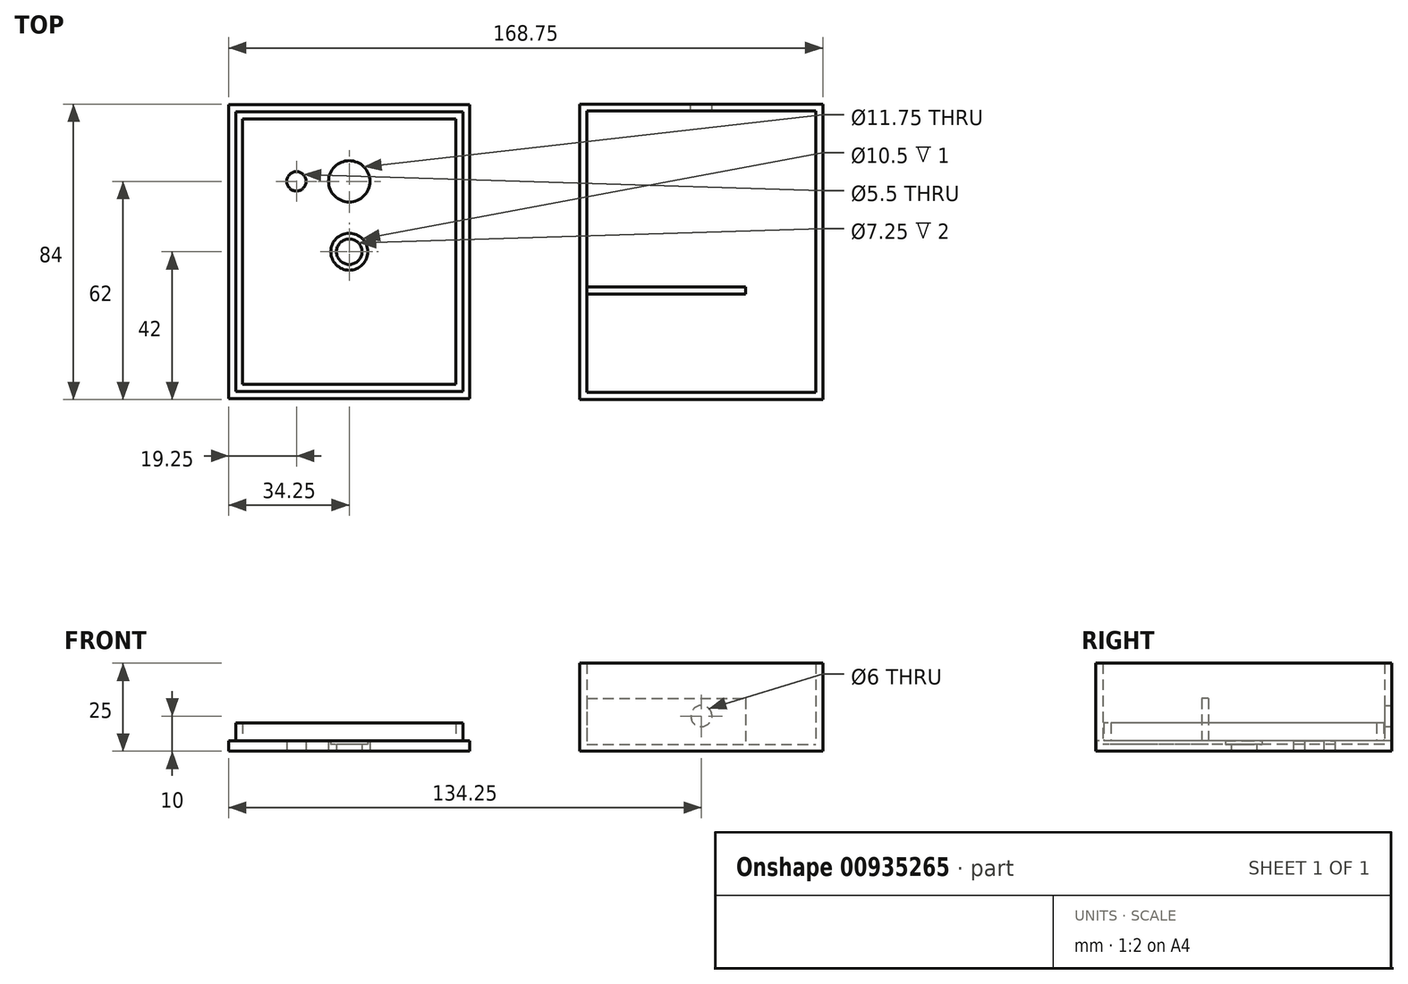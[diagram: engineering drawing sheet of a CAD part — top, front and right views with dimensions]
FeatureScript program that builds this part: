
annotation { "Feature Type Name" : "Feature", "Feature Type Description" : "" }
export const myFeature = defineFeature(function(context is Context, id is Id, definition is map)
    precondition{}
    {
        {
            var Q0;
            Q0=qCreatedBy(makeId("Top.planeOp"),FACE);
            var sketch = newSketch(context, id + "F0", { "sketchPlane" : qUnion([Q0])});
            skLineSegment(sketch, "E0.bottom", {"start": v(-32.5, 40) * mm, "end": v(32.5, 40) * mm});
            skLineSegment(sketch, "E0.top", {"start": v(-32.5, -40) * mm, "end": v(32.5, -40) * mm});
            skLineSegment(sketch, "E0.left", {"start": v(-32.5, 40) * mm, "end": v(-32.5, -40) * mm});
            skLineSegment(sketch, "E0.right", {"start": v(32.5, 40) * mm, "end": v(32.5, -40) * mm});
            skPoint(sketch, "E0.middle", {"position": v(0, 0) * mm});
            skLineSegment(sketch, "E1.0", {"start": v(-34.5, 42) * mm, "end": v(34.5, 42) * mm});
            skLineSegment(sketch, "E1.1", {"start": v(-34.5, 42) * mm, "end": v(-34.5, -42) * mm});
            skLineSegment(sketch, "E1.2", {"start": v(-34.5, -42) * mm, "end": v(34.5, -42) * mm});
            skLineSegment(sketch, "E1.3", {"start": v(34.5, 42) * mm, "end": v(34.5, -42) * mm});
            skLineSegment(sketch, "E2.bottom", {"start": v(-32.5, -10) * mm, "end": v(12.5, -10) * mm});
            skLineSegment(sketch, "E2.top", {"start": v(-32.5, -12) * mm, "end": v(12.5, -12) * mm});
            skLineSegment(sketch, "E2.left", {"start": v(-32.5, -10) * mm, "end": v(-32.5, -12) * mm});
            skLineSegment(sketch, "E2.right", {"start": v(12.5, -10) * mm, "end": v(12.5, -12) * mm});
            skLineSegment(sketch, "E3.bottom", {"start": v(-67.75, 39.75) * mm, "end": v(-132.25, 39.75) * mm});
            skLineSegment(sketch, "E3.top", {"start": v(-67.75, -39.75) * mm, "end": v(-132.25, -39.75) * mm});
            skLineSegment(sketch, "E3.left", {"start": v(-67.75, 39.75) * mm, "end": v(-67.75, -39.75) * mm});
            skLineSegment(sketch, "E3.right", {"start": v(-132.25, 39.75) * mm, "end": v(-132.25, -39.75) * mm});
            skPoint(sketch, "E3.middle", {"position": v(-100, 0) * mm});
            skLineSegment(sketch, "E4.0", {"start": v(-65.75, 41.75) * mm, "end": v(-134.25, 41.75) * mm});
            skLineSegment(sketch, "E4.1", {"start": v(-65.75, 41.75) * mm, "end": v(-65.75, -41.75) * mm});
            skLineSegment(sketch, "E4.2", {"start": v(-65.75, -41.75) * mm, "end": v(-134.25, -41.75) * mm});
            skLineSegment(sketch, "E4.3", {"start": v(-134.25, 41.75) * mm, "end": v(-134.25, -41.75) * mm});
            skLineSegment(sketch, "E5.0", {"start": v(-69.75, 37.75) * mm, "end": v(-130.25, 37.75) * mm});
            skLineSegment(sketch, "E5.1", {"start": v(-69.75, 37.75) * mm, "end": v(-69.75, -37.75) * mm});
            skLineSegment(sketch, "E5.2", {"start": v(-69.75, -37.75) * mm, "end": v(-130.25, -37.75) * mm});
            skLineSegment(sketch, "E5.3", {"start": v(-130.25, 37.75) * mm, "end": v(-130.25, -37.75) * mm});
            skCircle(sketch, "E6", {"center": v(-100, 20) * mm, "radius": 5.88 * mm});
            skCircle(sketch, "E7", {"center": v(-100, 0) * mm, "radius": 3.62 * mm});
            skCircle(sketch, "E8", {"center": v(-100, 0) * mm, "radius": 5.25 * mm});
            skCircle(sketch, "E9", {"center": v(-115, 20) * mm, "radius": 2.75 * mm});
            skSolve(sketch);
        }
        {
            var Q0;
            {var subQ4=sQuery(id+"F0.wireOp",EDGE,"E0.bottom");Q0=makeQuery(id+"F0.imprint","IMPRINT",FACE,{"disambiguationData":[TD([[makeQuery(id+"F0.imprint","IMPRINT",EDGE,{"derivedFrom":subQ4}),-1.0]])]});}
            extrude(context, id + "F1", {"entities" : qUnion([Q0]), "depth" : 2 * mm, "offsetDistance" : 25 * mm});
        }
        {
            var Q0;
            {var subQ3=sQuery(id+"F0.wireOp",EDGE,"E0.bottom");Q0=makeQuery(id+"F0.imprint","IMPRINT",FACE,{"disambiguationData":[TD([[makeQuery(id+"F0.imprint","IMPRINT",EDGE,{"derivedFrom":subQ3}),1.0]])]});}
            extrude(context, id + "F2", {"entities" : qUnion([Q0]), "operationType" : NewBodyOperationType.ADD, "depth" : 25 * mm, "offsetDistance" : 25 * mm});
        }
        {
            var Q0;
            Q0=makeQuery(id+"F0.imprint","IMPRINT",FACE,{"disambiguationData":[TD([[makeQuery(id+"F0.imprint","IMPRINT",EDGE,{"derivedFrom":sQuery(id+"F0.wireOp",EDGE,"E2.bottom")}),-1.0]])]});
            extrude(context, id + "F3", {"entities" : qUnion([Q0]), "operationType" : NewBodyOperationType.ADD, "depth" : 15 * mm, "offsetDistance" : 25 * mm});
        }
        {
            var Q0;
            Q0=makeQuery(id+"F0.imprint","IMPRINT",FACE,{"disambiguationData":[TD([[makeQuery(id+"F0.imprint","IMPRINT",EDGE,{"derivedFrom":sQuery(id+"F0.wireOp",EDGE,"E5.0")}),1.0]])]});
            var Q1;
            Q1=makeQuery(id+"F0.imprint","IMPRINT",FACE,{"disambiguationData":[TD([[makeQuery(id+"F0.imprint","IMPRINT",EDGE,{"derivedFrom":sQuery(id+"F0.wireOp",EDGE,"E3.bottom")}),-1.0]])]});
            extrude(context, id + "F4", {"entities" : qUnion([Q0, Q1]), "depth" : 3 * mm, "offsetDistance" : 25 * mm});
        }
        {
            var Q0;
            Q0=makeQuery(id+"F0.imprint","IMPRINT",FACE,{"disambiguationData":[TD([[makeQuery(id+"F0.imprint","IMPRINT",EDGE,{"derivedFrom":sQuery(id+"F0.wireOp",EDGE,"E3.bottom")}),1.0]])]});
            extrude(context, id + "F5", {"entities" : qUnion([Q0]), "operationType" : NewBodyOperationType.ADD, "depth" : 8 * mm, "offsetDistance" : 25 * mm});
        }
        {
            var Q0;
            Q0=makeQuery(id+"F0.imprint","IMPRINT",FACE,{"disambiguationData":[TD([[makeQuery(id+"F0.imprint","IMPRINT",EDGE,{"derivedFrom":sQuery(id+"F0.wireOp",EDGE,"E7")}),-1.0]])]});
            extrude(context, id + "F6", {"entities" : qUnion([Q0]), "operationType" : NewBodyOperationType.ADD, "depth" : 2 * mm, "offsetDistance" : 25 * mm});
        }
        {
            var Q0;
            Q0=makeQuery(id+"F2.opExtrude","SWEPT_FACE",FACE,{"disambiguationData":[OSD([sQuery(id+"F0.wireOp",EDGE,"E1.0")])]});
            var sketch = newSketch(context, id + "F7", { "sketchPlane" : qUnion([Q0])});
            skCircle(sketch, "E10", {"center": v(0, 10) * mm, "radius": 3 * mm});
            skSolve(sketch);
        }
        {
            var Q0;
            Q0=makeQuery(id+"F7.imprint","IMPRINT",FACE,{"disambiguationData":[TD([[makeQuery(id+"F7.imprint","IMPRINT",EDGE,{"derivedFrom":sQuery(id+"F7.wireOp",EDGE,"E10")}),1.0]])]});
            extrude(context, id + "F8", {"entities" : qUnion([Q0]), "operationType" : NewBodyOperationType.REMOVE, "endBound" : BoundingType.UP_TO_NEXT, "oppositeDirection" : true, "depth" : 25 * mm, "offsetDistance" : 25 * mm});
        }
    });
